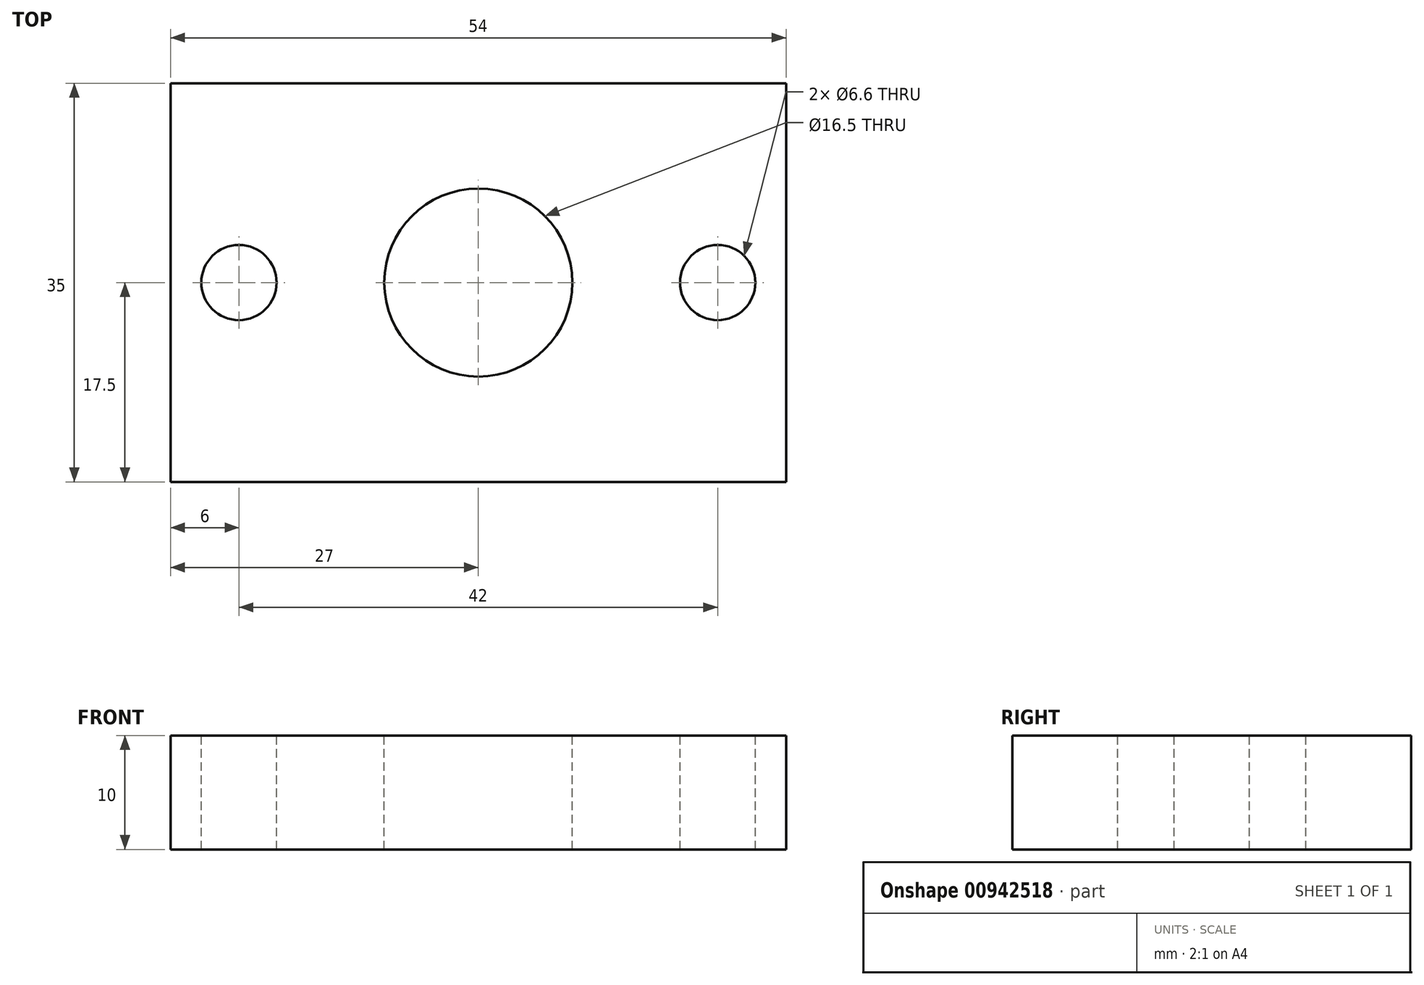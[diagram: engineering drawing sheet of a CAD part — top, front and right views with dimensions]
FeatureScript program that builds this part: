
annotation { "Feature Type Name" : "Feature", "Feature Type Description" : "" }
export const myFeature = defineFeature(function(context is Context, id is Id, definition is map)
    precondition{}
    {
        {
            var Q0;
            Q0=qCreatedBy(makeId("Top.planeOp"),FACE);
            var sketch = newSketch(context, id + "F0", { "sketchPlane" : qUnion([Q0])});
            skLineSegment(sketch, "E0.bottom", {"start": v(27, -17.5) * mm, "end": v(-27, -17.5) * mm});
            skLineSegment(sketch, "E0.top", {"start": v(27, 17.5) * mm, "end": v(-27, 17.5) * mm});
            skLineSegment(sketch, "E0.left", {"start": v(27, -17.5) * mm, "end": v(27, 17.5) * mm});
            skLineSegment(sketch, "E0.right", {"start": v(-27, -17.5) * mm, "end": v(-27, 17.5) * mm});
            skPoint(sketch, "E0.middle", {"position": v(0, 0) * mm});
            skSolve(sketch);
        }
        {
            var Q0;
            Q0=makeQuery(id+"F0.imprint","IMPRINT",FACE,{"disambiguationData":[TD([[makeQuery(id+"F0.imprint","IMPRINT",EDGE,{"derivedFrom":sQuery(id+"F0.wireOp",EDGE,"E0.bottom")}),-1.0]])]});
            extrude(context, id + "F1", {"entities" : qUnion([Q0]), "depth" : 10 * mm, "offsetDistance" : 25 * mm});
        }
        {
            var Q0;
            Q0=makeQuery(id+"F1.opExtrude","CAP_FACE",FACE,{"disambiguationData":[OSD([sQuery(id+"F0.wireOp",EDGE,"E0.bottom"),sQuery(id+"F0.wireOp",EDGE,"E0.top"),sQuery(id+"F0.wireOp",EDGE,"E0.left"),sQuery(id+"F0.wireOp",EDGE,"E0.right")])],"isStart":false});
            var sketch = newSketch(context, id + "F2", { "sketchPlane" : qUnion([Q0])});
            skPoint(sketch, "E1", {"position": v(0, 0) * mm});
            skSolve(sketch);
        }
        {
            var Q0;
            Q0=sQuery(id+"F2.wireOp",VERTEX,"E1");
            var Q1;
            Q1=makeQuery(id+"F1.opExtrude","SWEPT_BODY",BODY,{"disambiguationData":[OSD([sQuery(id+"F0.wireOp",EDGE,"E0.bottom"),sQuery(id+"F0.wireOp",EDGE,"E0.top"),sQuery(id+"F0.wireOp",EDGE,"E0.left"),sQuery(id+"F0.wireOp",EDGE,"E0.right")])]});
            hole(context, id + "F3", {"style" : HoleStyle.SIMPLE, "endStyle" : HoleEndStyle.THROUGH, "standardTappedOrClearance" : lookupTablePath({ "standard" : "ISO", "engagement" : "75%", "pitch" : "1.5 mm", "size" : "M18", "type" : "Tapped" }), "standardBlindInLast" : lookupTablePath({ "standard" : "ISO", "fit" : "Normal", "engagement" : "75%", "pitch" : "1.5 mm", "size" : "M18", "type" : "Clearance & tapped" }), "holeDiameter" : 16.5 * mm, "majorDiameter" : 18 * mm, "showTappedDepth" : true, "isTappedThrough" : true, "tappedDepth" : 5.5 * mm, "tapClearance" : 3, "locations" : qUnion([Q0]), "scope" : qUnion([Q1])});
        }
        {
            var Q0;
            Q0=makeQuery(id+"F1.opExtrude","CAP_FACE",FACE,{"disambiguationData":[OSD([sQuery(id+"F0.wireOp",EDGE,"E0.bottom"),sQuery(id+"F0.wireOp",EDGE,"E0.top"),sQuery(id+"F0.wireOp",EDGE,"E0.left"),sQuery(id+"F0.wireOp",EDGE,"E0.right")])],"isStart":false});
            var sketch = newSketch(context, id + "F4", { "sketchPlane" : qUnion([Q0])});
            skLineSegment(sketch, "E2", {"start": v(-27, 0) * mm, "end": v(0, 0) * mm});
            skLineSegment(sketch, "E3", {"start": v(0, 0) * mm, "end": v(27, 0) * mm});
            skPoint(sketch, "E4", {"position": v(-21, 0) * mm});
            skPoint(sketch, "E5", {"position": v(21, 0) * mm});
            skSolve(sketch);
        }
        {
            var Q0;
            Q0=sQuery(id+"F4.wireOp",VERTEX,"E4");
            var Q1;
            Q1=sQuery(id+"F4.wireOp",VERTEX,"E5");
            var Q2;
            Q2=makeQuery(id+"F1.opExtrude","SWEPT_BODY",BODY,{"disambiguationData":[OSD([sQuery(id+"F0.wireOp",EDGE,"E0.bottom"),sQuery(id+"F0.wireOp",EDGE,"E0.top"),sQuery(id+"F0.wireOp",EDGE,"E0.left"),sQuery(id+"F0.wireOp",EDGE,"E0.right")])]});
            hole(context, id + "F5", {"style" : HoleStyle.SIMPLE, "endStyle" : HoleEndStyle.THROUGH, "standardTappedOrClearance" : lookupTablePath({ "fit" : "Normal", "standard" : "ISO", "size" : "M6", "type" : "Clearance" }), "standardBlindInLast" : lookupTablePath({ "fit" : "Normal", "standard" : "ISO", "engagement" : "75%", "pitch" : "1 mm", "size" : "M6", "type" : "Clearance & tapped" }), "holeDiameter" : 6.6 * mm, "majorDiameter" : 6 * mm, "isTappedThrough" : true, "tappedDepth" : 5.5 * mm, "tapClearance" : 3, "locations" : qUnion([Q0, Q1]), "scope" : qUnion([Q2])});
        }
    });
